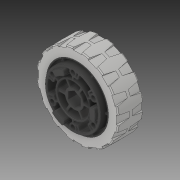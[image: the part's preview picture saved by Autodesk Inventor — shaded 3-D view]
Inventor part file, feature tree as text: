
AUTODESK INVENTOR PART (.ipt)
format: ipt  version: 2019 (Build 230136000, 136)  size: 3,140,608 bytes
history: native  units: in
note: dims shown in document units (in); Inventor stores cm internally (conversion verified against a paired STEP export)
features: fillet x2
ambient origin geometry x8: Origin, YZ Plane, XZ Plane, XY Plane, X Axis, Y Axis, Z Axis, Center Point
bodies: Solid1 (feature_tree), Solid2 (feature_tree)
feature tree (2):
  fillet  "Fillet6"  [1 undecoded]
  fillet  "Fillet7"  [1 undecoded]
note: 2 required parameter values undecoded (feature->parameter linkage not recoverable at this tier; creation-order binding heuristic only, values carry confidence <= 0.55)
